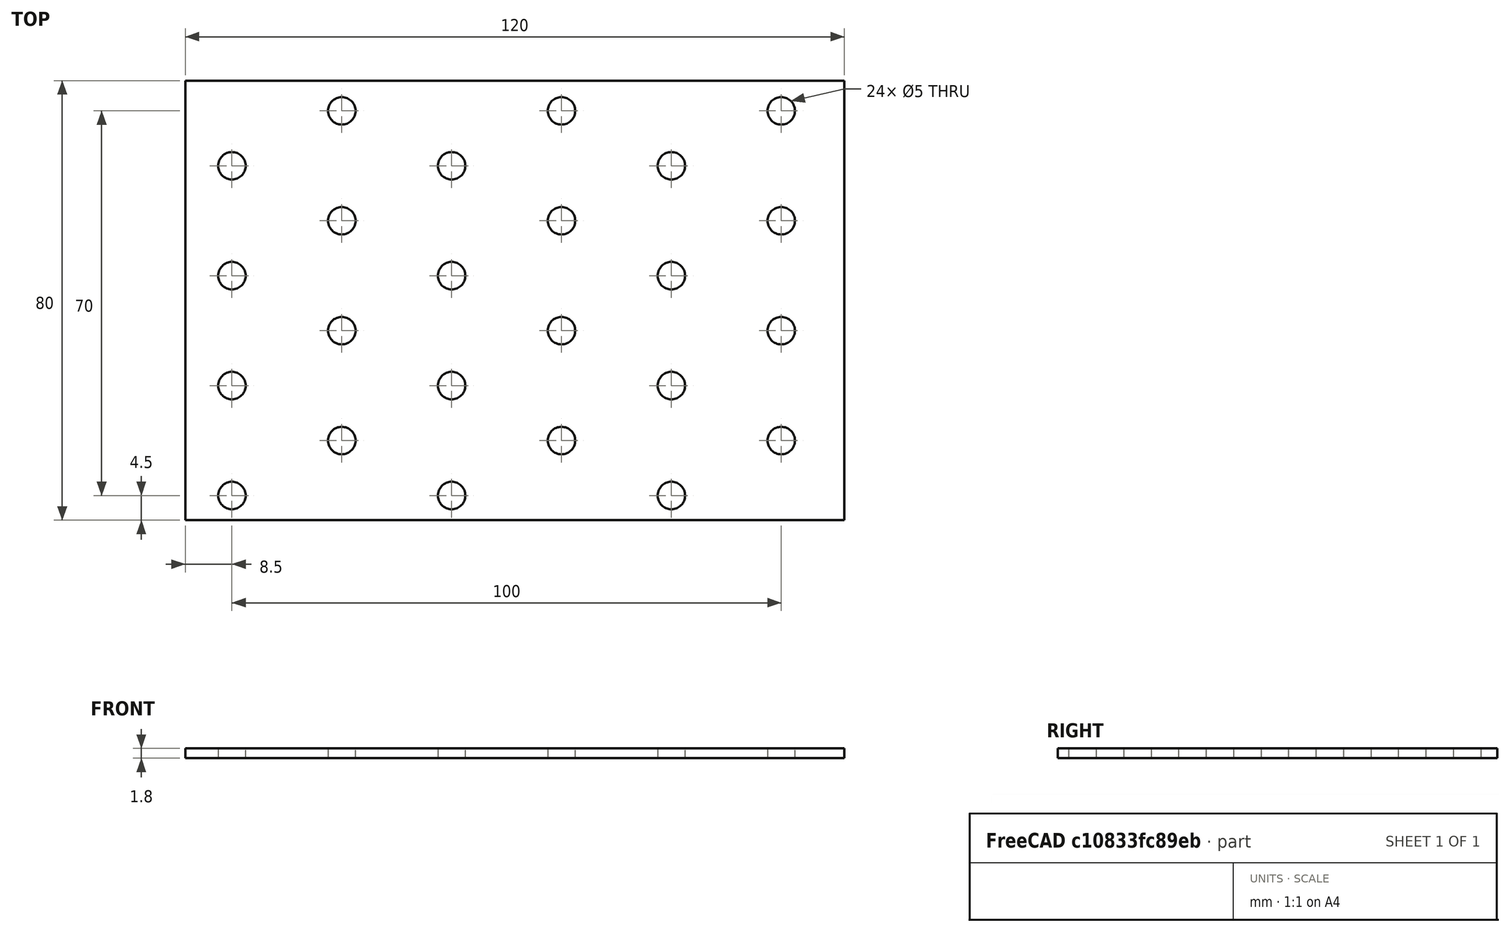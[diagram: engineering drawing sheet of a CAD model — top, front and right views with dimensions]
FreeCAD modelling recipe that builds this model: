
FCSTD DOCUMENT  (FreeCAD 0.19R24276 (Git))
Label: Bar_80x120__1_8mm
License: All rights reserved
LicenseURL: http://en.wikipedia.org/wiki/All_rights_reserved
objects: Sketcher::SketchObject×1, PartDesign::Pad×1, PartDesign::Body×1
note: 4 computed .brp shape members not serialized (recipe doc carries the construction recipe); baked Part::Feature solids carry a one-line shape summary decoded from their .brp

FEATURE [Sketcher::SketchObject] Sketch
  FullyConstrained = true
  MapMode = 5
  Support = -> [XY_Plane]
  sketch-geometry (46):
    g0: LineSegment StartX=0 StartY=0 StartZ=0 EndX=120 EndY=0 EndZ=0
    g1: LineSegment StartX=120 StartY=0 StartZ=0 EndX=120 EndY=80 EndZ=0
    g2: LineSegment StartX=120 StartY=80 StartZ=0 EndX=0 EndY=80 EndZ=0
    g3: LineSegment StartX=0 StartY=80 StartZ=0 EndX=0 EndY=0 EndZ=0
    g4: LineSegment StartX=0 StartY=4.5 StartZ=0 EndX=120 EndY=4.5 EndZ=0
    g5: LineSegment StartX=0 StartY=24.5 StartZ=0 EndX=120 EndY=24.5 EndZ=0
    g6: LineSegment StartX=0 StartY=44.5 StartZ=0 EndX=120 EndY=44.5 EndZ=0
    g7: LineSegment StartX=0 StartY=64.5 StartZ=0 EndX=120 EndY=64.5 EndZ=0
    g8: LineSegment StartX=48.5 StartY=0 StartZ=0 EndX=48.5 EndY=4.5 EndZ=0
    g9: LineSegment StartX=68.5 StartY=0 StartZ=0 EndX=68.5 EndY=4.5 EndZ=0
    g10: LineSegment StartX=88.5 StartY=0 StartZ=0 EndX=88.5 EndY=4.5 EndZ=0
    g11: LineSegment StartX=108.5 StartY=0 StartZ=0 EndX=108.5 EndY=4.5 EndZ=0
    g12: LineSegment StartX=0 StartY=14.5 StartZ=0 EndX=120 EndY=14.5 EndZ=0
    g13: LineSegment StartX=0 StartY=34.5 StartZ=0 EndX=120 EndY=34.5 EndZ=0
    g14: LineSegment StartX=0 StartY=54.5 StartZ=0 EndX=120 EndY=54.5 EndZ=0
    g15: LineSegment StartX=0 StartY=74.5 StartZ=0 EndX=120 EndY=74.5 EndZ=0
    g16: LineSegment StartX=48.5 StartY=24.5 StartZ=0 EndX=48.5 EndY=80 EndZ=0
    g17: LineSegment StartX=68.5 StartY=14.5 StartZ=0 EndX=68.5 EndY=80 EndZ=0
    g18: LineSegment StartX=88.5 StartY=24.5 StartZ=0 EndX=88.5 EndY=80 EndZ=0
    g19: LineSegment StartX=108.5 StartY=14.5 StartZ=0 EndX=108.5 EndY=80 EndZ=0
    g20: Circle CenterX=8.5 CenterY=4.5 CenterZ=0 NormalX=0 NormalY=0 NormalZ=1 AngleXU=0 Radius=2.5
    g21: Circle CenterX=48.5 CenterY=4.5 CenterZ=0 NormalX=0 NormalY=0 NormalZ=1 AngleXU=0 Radius=2.5
    g22: Circle CenterX=88.5 CenterY=4.5 CenterZ=0 NormalX=0 NormalY=0 NormalZ=1 AngleXU=0 Radius=2.5
    g23: Circle CenterX=28.5 CenterY=14.5 CenterZ=0 NormalX=0 NormalY=0 NormalZ=1 AngleXU=0 Radius=2.5
    g24: Circle CenterX=108.5 CenterY=14.5 CenterZ=0 NormalX=0 NormalY=0 NormalZ=1 AngleXU=0 Radius=2.5
    g25: Circle CenterX=8.5 CenterY=24.5 CenterZ=0 NormalX=0 NormalY=0 NormalZ=1 AngleXU=0 Radius=2.5
    g26: Circle CenterX=48.5 CenterY=24.5 CenterZ=0 NormalX=0 NormalY=0 NormalZ=1 AngleXU=0 Radius=2.5
    g27: Circle CenterX=88.5 CenterY=24.5 CenterZ=0 NormalX=0 NormalY=0 NormalZ=1 AngleXU=0 Radius=2.5
    g28: Circle CenterX=8.5 CenterY=44.5 CenterZ=0 NormalX=0 NormalY=0 NormalZ=1 AngleXU=0 Radius=2.5
    g29: Circle CenterX=48.5 CenterY=44.5 CenterZ=0 NormalX=0 NormalY=0 NormalZ=1 AngleXU=0 Radius=2.5
    g30: Circle CenterX=88.5 CenterY=44.5 CenterZ=0 NormalX=0 NormalY=0 NormalZ=1 AngleXU=0 Radius=2.5
    g31: Circle CenterX=28.5 CenterY=54.5 CenterZ=0 NormalX=0 NormalY=0 NormalZ=1 AngleXU=0 Radius=2.5
    g32: Circle CenterX=68.5 CenterY=54.5 CenterZ=0 NormalX=0 NormalY=0 NormalZ=1 AngleXU=0 Radius=2.5
    g33: Circle CenterX=108.5 CenterY=54.5 CenterZ=0 NormalX=0 NormalY=0 NormalZ=1 AngleXU=0 Radius=2.5
    g34: Circle CenterX=88.5 CenterY=64.5 CenterZ=0 NormalX=0 NormalY=0 NormalZ=1 AngleXU=0 Radius=2.5
    g35: Circle CenterX=48.5 CenterY=64.5 CenterZ=0 NormalX=0 NormalY=0 NormalZ=1 AngleXU=0 Radius=2.5
    g36: Circle CenterX=8.5 CenterY=64.5 CenterZ=0 NormalX=0 NormalY=0 NormalZ=1 AngleXU=0 Radius=2.5
    g37: Circle CenterX=28.5 CenterY=34.5 CenterZ=0 NormalX=0 NormalY=0 NormalZ=1 AngleXU=0 Radius=2.5
    g38: Circle CenterX=68.5 CenterY=34.5 CenterZ=0 NormalX=0 NormalY=0 NormalZ=1 AngleXU=0 Radius=2.5
    g39: Circle CenterX=108.5 CenterY=34.5 CenterZ=0 NormalX=0 NormalY=0 NormalZ=1 AngleXU=0 Radius=2.5
    g40: Circle CenterX=28.5 CenterY=74.5 CenterZ=0 NormalX=0 NormalY=0 NormalZ=1 AngleXU=0 Radius=2.5
    g41: Circle CenterX=68.5 CenterY=74.5 CenterZ=0 NormalX=0 NormalY=0 NormalZ=1 AngleXU=0 Radius=2.5
    g42: Circle CenterX=108.5 CenterY=74.5 CenterZ=0 NormalX=0 NormalY=0 NormalZ=1 AngleXU=0 Radius=2.5
    g43: LineSegment StartX=28.5 StartY=74.5 StartZ=0 EndX=28.5 EndY=14.5 EndZ=0
    g44: LineSegment StartX=8.5 StartY=4.5 StartZ=0 EndX=8.5 EndY=24.5 EndZ=0
    g45: Circle CenterX=68.5 CenterY=14.5 CenterZ=0 NormalX=0 NormalY=0 NormalZ=1 AngleXU=0 Radius=2.5
  constraints (143):
    c: Coincident(g0,g1)
    c: Coincident(g1,g2)
    c: Coincident(g2,g3)
    c: Coincident(g3,g0)
    c: Horizontal(g0)
    c: Horizontal(g2)
    c: Vertical(g1)
    c: Vertical(g3)
    c: Coincident(g0,g-1)
    c: DistanceX(g0,g0) = 120
    c: DistanceY(g3,g3) = 80
    c: Horizontal(g4)
    c: PointOnObject(g4,g3)
    c: PointOnObject(g4,g1)
    c: Horizontal(g5)
    c: PointOnObject(g5,g3)
    c: PointOnObject(g5,g1)
    c: DistanceY(g4,g5) = 20
    c: Horizontal(g6)
    c: PointOnObject(g6,g1)
    c: PointOnObject(g6,g3)
    c: DistanceY(g5,g6) = 20
    c: Horizontal(g7)
    c: PointOnObject(g7,g1)
    c: PointOnObject(g7,g3)
    c: DistanceY(g6,g7) = 20
    c: Vertical(g8)
    c: Vertical(g9)
    c: Vertical(g10)
    c: Vertical(g11)
    c: PointOnObject(g8,g0)
    c: PointOnObject(g9,g0)
    c: PointOnObject(g10,g0)
    c: PointOnObject(g11,g0)
    c: PointOnObject(g19,g2)
    c: PointOnObject(g18,g2)
    c: PointOnObject(g17,g2)
    c: PointOnObject(g16,g2)
    c: DistanceX(g8,g9) = 20
    c: DistanceX(g9,g10) = 20
    c: DistanceX(g10,g11) = 20
    c: Horizontal(g12)
    c: Horizontal(g13)
    c: Horizontal(g14)
    c: Horizontal(g15)
    c: PointOnObject(g12,g3)
    c: PointOnObject(g13,g3)
    c: PointOnObject(g14,g3)
    c: PointOnObject(g15,g3)
    c: PointOnObject(g15,g1)
    c: PointOnObject(g14,g1)
    c: PointOnObject(g13,g1)
    c: PointOnObject(g12,g1)
    c: DistanceY(g0,g12) = 14.5
    c: DistanceY(g12,g13) = 20
    c: DistanceY(g13,g14) = 20
    c: DistanceY(g14,g15) = 20
    c: PointOnObject(g20,g4)
    c: PointOnObject(g23,g12)
    c: PointOnObject(g8,g4)
    c: Tangent(g8,g16)
    c: PointOnObject(g9,g4)
    c: PointOnObject(g17,g12)
    c: Tangent(g9,g17)
    c: PointOnObject(g10,g4)
    c: Tangent(g10,g18)
    c: PointOnObject(g11,g4)
    c: PointOnObject(g19,g12)
    c: Tangent(g11,g19)
    c: Coincident(g21,g8)
    c: Coincident(g22,g10)
    c: Coincident(g24,g19)
    c: Equal(g20,g23)
    c: Equal(g23,g21)
    c: Equal(g21,g22)
    c: Equal(g22,g24)
    c: Diameter(g23) = 5
    c: PointOnObject(g16,g5)
    c: PointOnObject(g18,g5)
    c: Equal(g26,g27)
    c: Equal(g36,g31)
    c: Equal(g31,g35)
    c: Equal(g35,g34)
    c: Equal(g34,g33)
    c: Diameter(g31) = 5
    c: Equal(g34,g32)
    c: Equal(g29,g30)
    c: Diameter(g37) = 5
    c: Diameter(g40) = 5
    c: Coincident(g43,g40)
    c: Coincident(g43,g23)
    c: Vertical(g43)
    c: DistanceX(g20,g23) = 20
    c: DistanceX(g0,g20) = 8.5
    c: DistanceY(g0,g4) = 4.5
    c: Coincident(g44,g20)
    c: Coincident(g44,g25)
    c: Vertical(g44)
    c: Coincident(g45,g17)
    c: Equal(g24,g45)
    c: Vertical(g24,g39)
    c: Vertical(g39,g33)
    c: Vertical(g33,g42)
    c: Vertical(g34,g30)
    c: Vertical(g30,g27)
    c: Vertical(g27,g22)
    c: Vertical(g41,g32)
    c: Vertical(g32,g38)
    c: Vertical(g38,g45)
    c: Vertical(g21,g26)
    c: Vertical(g26,g29)
    c: Vertical(g29,g35)
    c: Vertical(g23,g37)
    c: Vertical(g37,g31)
    c: Vertical(g36,g28)
    c: Vertical(g28,g25)
    c: Horizontal(g25,g27)
    c: Horizontal(g27,g26)
    c: DistanceX(g23,g8) = 20
    c: Horizontal(g27,g5)
    c: Equal(g25,g20)
    c: Equal(g27,g25)
    c: Horizontal(g37,g38)
    c: Horizontal(g38,g39)
    c: Horizontal(g39,g13)
    c: Equal(g37,g38)
    c: Equal(g38,g39)
    c: Horizontal(g28,g29)
    c: Horizontal(g29,g30)
    c: Horizontal(g30,g6)
    c: Equal(g28,g29)
    c: Equal(g30,g38)
    c: Horizontal(g31,g32)
    c: Horizontal(g32,g33)
    c: Horizontal(g33,g14)
    c: Horizontal(g36,g35)
    c: Horizontal(g35,g34)
    c: Horizontal(g34,g7)
    c: Horizontal(g40,g41)
    c: Horizontal(g41,g42)
    c: Equal(g40,g41)
    c: Equal(g41,g42)
    c: Horizontal(g42,g15)
FEATURE [PartDesign::Pad] Pad
  Direction = (1,1,1)
  Length = 1.8
  Length2 = 100
  Profile = -> Sketch
  Type = 0
FEATURE [PartDesign::Body] Body
  Group = -> [Sketch,Pad]
  Origin = -> Origin
  Tip = -> Pad
